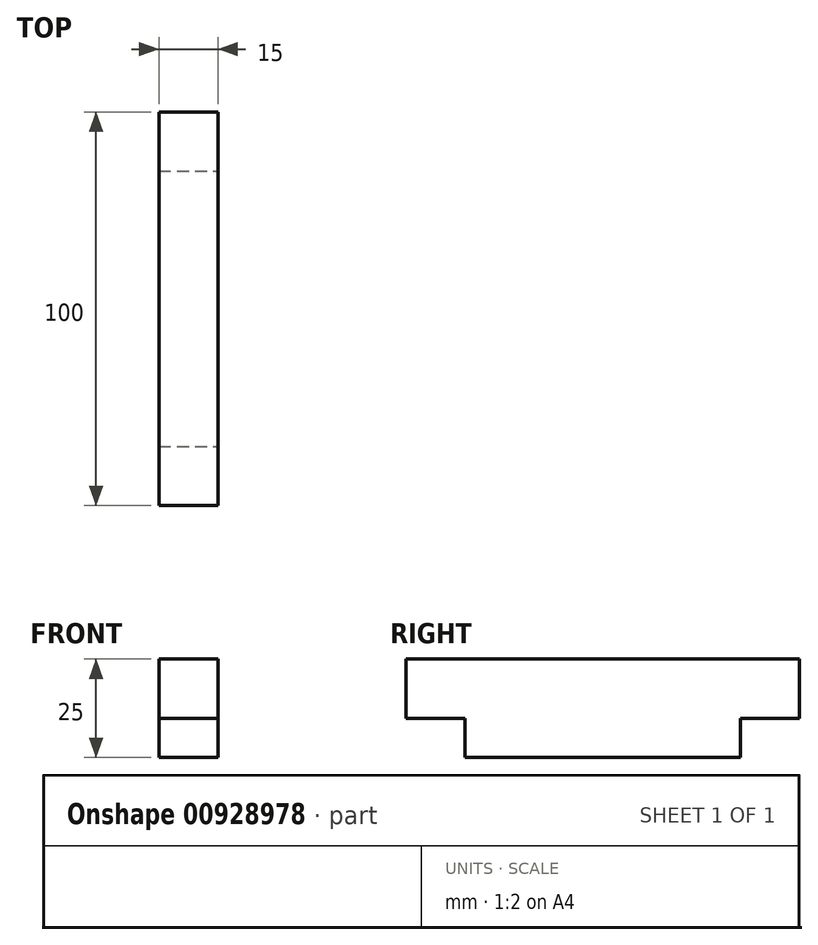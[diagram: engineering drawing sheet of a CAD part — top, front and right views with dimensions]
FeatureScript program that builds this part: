
annotation { "Feature Type Name" : "Feature", "Feature Type Description" : "" }
export const myFeature = defineFeature(function(context is Context, id is Id, definition is map)
    precondition{}
    {
        {
            var Q0;
            Q0=qCreatedBy(makeId("Front.planeOp"),FACE);
            var sketch = newSketch(context, id + "F0", { "sketchPlane" : qUnion([Q0])});
            skLineSegment(sketch, "E0.bottom", {"start": v(-7.6, 5.42) * mm, "end": v(7.4, 5.42) * mm});
            skLineSegment(sketch, "E0.top", {"start": v(-7.6, -19.58) * mm, "end": v(7.4, -19.58) * mm});
            skLineSegment(sketch, "E0.left", {"start": v(-7.6, 5.42) * mm, "end": v(-7.6, -19.58) * mm});
            skLineSegment(sketch, "E0.right", {"start": v(7.4, 5.42) * mm, "end": v(7.4, -19.58) * mm});
            skLineSegment(sketch, "E1.top", {"start": v(-7.6, -9.58) * mm, "end": v(7.4, -9.58) * mm});
            skLineSegment(sketch, "E1.left", {"start": v(-7.6, 5.42) * mm, "end": v(-7.6, -9.58) * mm});
            skLineSegment(sketch, "E1.right", {"start": v(7.4, 5.42) * mm, "end": v(7.4, -9.58) * mm});
            skSolve(sketch);
        }
        {
            var Q0;
            {var subQ0=sQuery(id+"F0.wireOp",EDGE,"E0.bottom");Q0=makeQuery(id+"F0.imprint","IMPRINT",FACE,{"disambiguationData":[TD([[makeQuery(id+"F0.imprint","IMPRINT",EDGE,{"derivedFrom":subQ0}),-1.0]])]});}
            extrude(context, id + "F1", {"entities" : qUnion([Q0]), "endBound" : BoundingType.SYMMETRIC, "depth" : 100 * mm, "offsetDistance" : 25 * mm});
        }
        {
            var Q0;
            {var subQ0=sQuery(id+"F0.wireOp",EDGE,"E0.top");Q0=makeQuery(id+"F0.imprint","IMPRINT",FACE,{"disambiguationData":[TD([[makeQuery(id+"F0.imprint","IMPRINT",EDGE,{"derivedFrom":subQ0}),1.0]])]});}
            extrude(context, id + "F2", {"entities" : qUnion([Q0]), "operationType" : NewBodyOperationType.ADD, "endBound" : BoundingType.SYMMETRIC, "depth" : 70 * mm, "offsetDistance" : 25 * mm});
        }
    });
